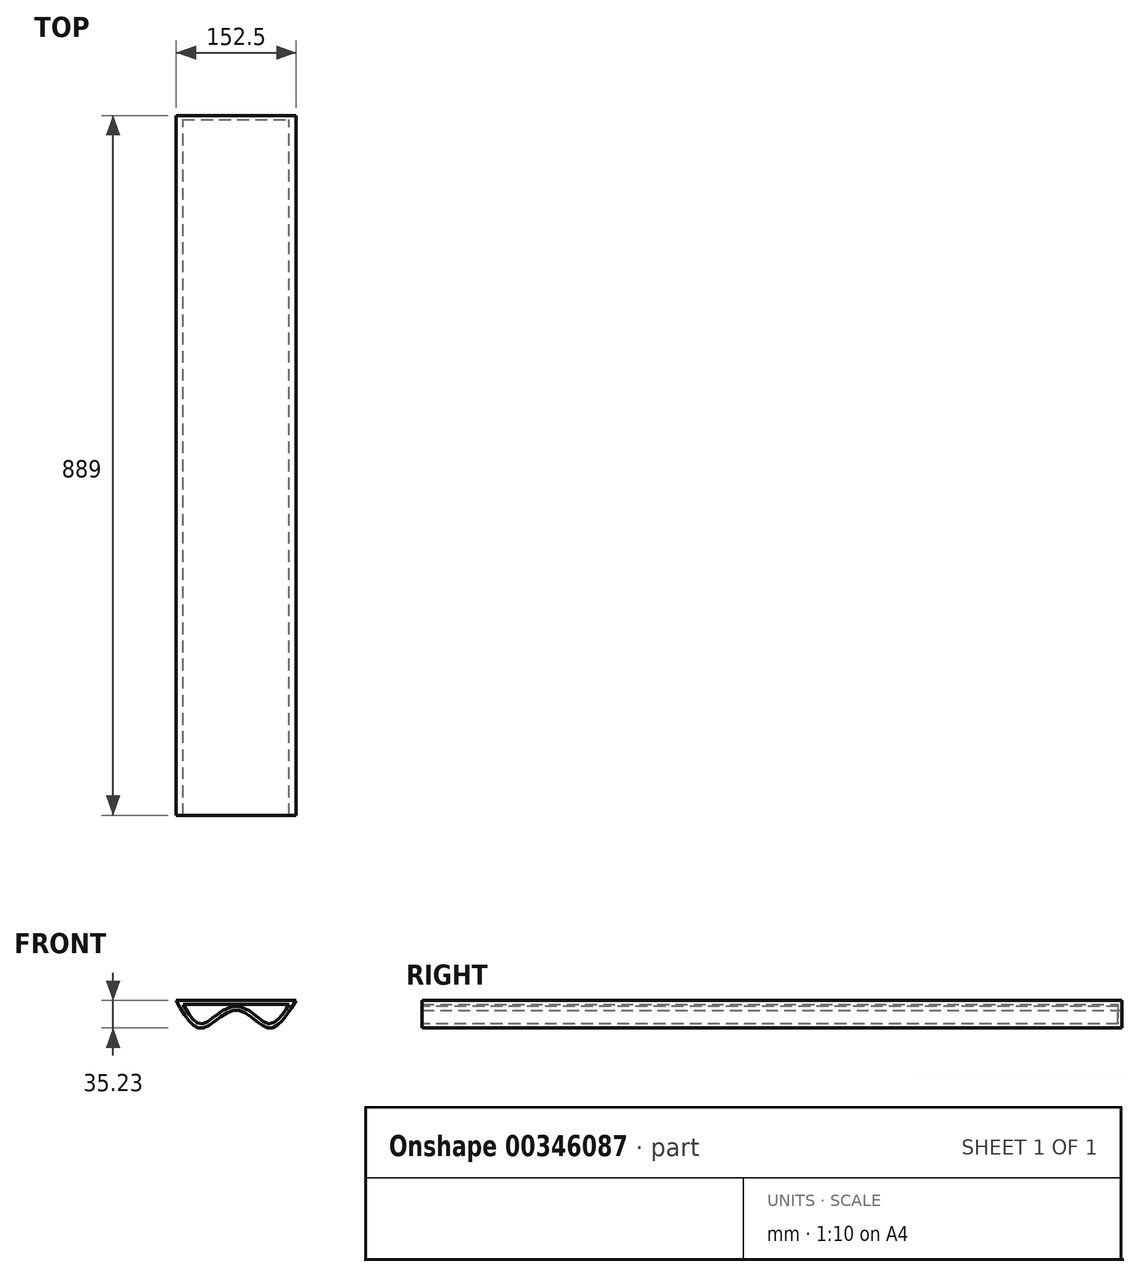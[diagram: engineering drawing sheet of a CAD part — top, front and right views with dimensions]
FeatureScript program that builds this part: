
annotation { "Feature Type Name" : "Feature", "Feature Type Description" : "" }
export const myFeature = defineFeature(function(context is Context, id is Id, definition is map)
    precondition{}
    {
        {
            var Q0;
            Q0=qCreatedBy(makeId("Front.planeOp"),FACE);
            var sketch = newSketch(context, id + "F0", { "sketchPlane" : qUnion([Q0])});
            skLineSegment(sketch, "E0", {"start": v(-76.25, 35.12) * mm, "end": v(76.25, 35.12) * mm});
            skFitSpline(sketch, "E1", {"points": [v(-76.25, 35.12) * mm, v(-43.4, 0) * mm, v(0, 22.56) * mm, v(41.12, 0) * mm, v(76.25, 35.12) * mm], "startDerivative": vector(120.96, -219.64) * mm, "endDerivative": vector(132.1, 218.3) * mm});
            skSolve(sketch);
        }
        {
            var Q0;
            Q0 = qSketchRegion(id + "F0", true);
            extrude(context, id + "F1", {"entities" : qUnion([Q0]), "depth" : 889 * mm});
        }
        {
            var Q0;
            Q0=makeQuery(id+"F1.opExtrude","CAP_FACE",FACE,{"disambiguationData":[OSD([sQuery(id+"F0.wireOp",EDGE,"E0"),sQuery(id+"F0.wireOp",EDGE,"E1")])],"isStart":false});
            shell(context, id + "F2", {"entities" : qUnion([Q0]), "thickness" : 5.08 * mm});
        }
    });
